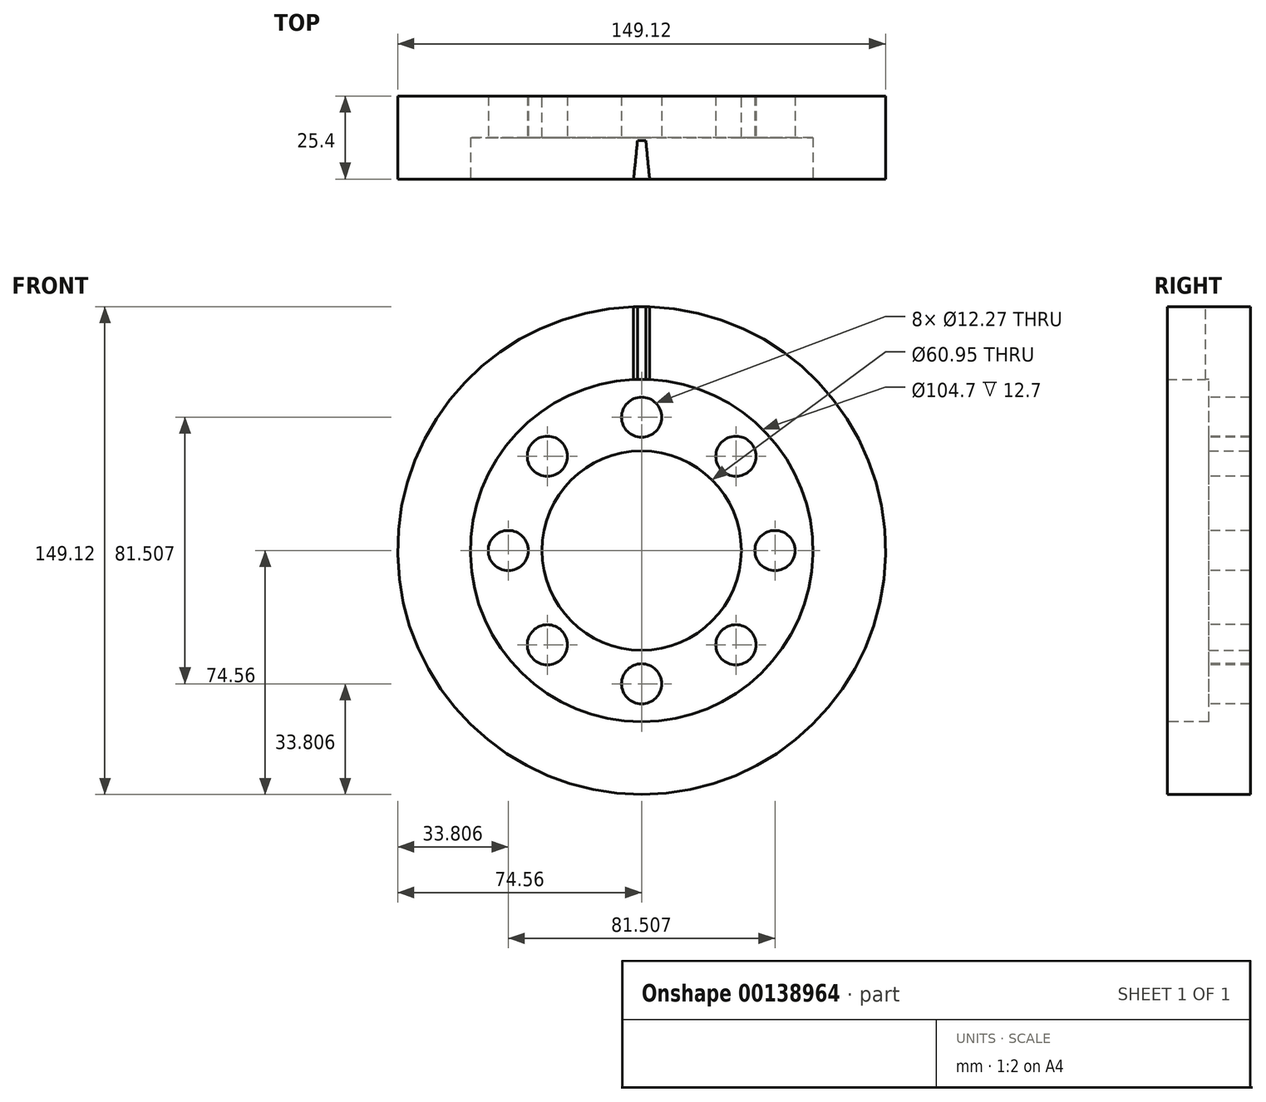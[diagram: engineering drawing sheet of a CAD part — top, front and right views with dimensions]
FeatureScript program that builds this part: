
annotation { "Feature Type Name" : "Feature", "Feature Type Description" : "" }
export const myFeature = defineFeature(function(context is Context, id is Id, definition is map)
    precondition{}
    {
        {
            var Q0;
            Q0=qCreatedBy(makeId("Front.planeOp"),FACE);
            var sketch = newSketch(context, id + "F0", { "sketchPlane" : qUnion([Q0])});
            skCircle(sketch, "E0", {"center": v(0, 0) * mm, "radius": 74.56 * mm});
            skCircle(sketch, "E1", {"center": v(0, 0) * mm, "radius": 30.48 * mm});
            skSolve(sketch);
        }
        {
            var Q0;
            Q0 = qSketchRegion(id + "F0", true);
            extrude(context, id + "F1", {"entities" : qUnion([Q0]), "depth" : 25.4 * mm});
        }
        {
            var Q0;
            Q0=makeQuery(id+"F1.opExtrude","CAP_FACE",FACE,{"disambiguationData":[OSD([sQuery(id+"F0.wireOp",EDGE,"E0"),sQuery(id+"F0.wireOp",EDGE,"E1")])],"isStart":false});
            var sketch = newSketch(context, id + "F2", { "sketchPlane" : qUnion([Q0])});
            skCircle(sketch, "E2", {"center": v(0, 0) * mm, "radius": 52.35 * mm});
            skSolve(sketch);
        }
        {
            var Q0;
            Q0 = qSketchRegion(id + "F2", true);
            extrude(context, id + "F3", {"entities" : qUnion([Q0]), "operationType" : NewBodyOperationType.REMOVE, "oppositeDirection" : true, "depth" : 12.7 * mm});
        }
        {
            var Q0;
            Q0=makeQuery(id+"F3.boolean.opBoolean","COPY",FACE,{"derivedFrom":makeQuery(id+"F3.opExtrude","CAP_FACE",FACE,{"disambiguationData":[OSD([sQuery(id+"F2.wireOp",EDGE,"E2")])],"isStart":false})});
            var sketch = newSketch(context, id + "F4", { "sketchPlane" : qUnion([Q0])});
            skCircle(sketch, "E3", {"center": v(0, 40.75) * mm, "radius": 6.13 * mm});
            skCircle(sketch, "E4.1.0", {"center": v(-28.82, 28.82) * mm, "radius": 6.13 * mm});
            skCircle(sketch, "E4.2.0", {"center": v(-40.75, 0) * mm, "radius": 6.13 * mm});
            skCircle(sketch, "E4.3.0", {"center": v(-28.82, -28.82) * mm, "radius": 6.13 * mm});
            skCircle(sketch, "E4.4.0", {"center": v(0, -40.75) * mm, "radius": 6.13 * mm});
            skCircle(sketch, "E4.5.0", {"center": v(28.82, -28.82) * mm, "radius": 6.13 * mm});
            skCircle(sketch, "E4.6.0", {"center": v(40.75, 0) * mm, "radius": 6.13 * mm});
            skCircle(sketch, "E4.7.0", {"center": v(28.82, 28.82) * mm, "radius": 6.13 * mm});
            skPoint(sketch, "E4.center", {"position": v(0, 0) * mm});
            skSolve(sketch);
        }
        {
            var Q0;
            Q0 = qSketchRegion(id + "F4", true);
            extrude(context, id + "F5", {"entities" : qUnion([Q0]), "operationType" : NewBodyOperationType.REMOVE, "oppositeDirection" : true, "depth" : 12.7 * mm});
        }
        {
            var Q0;
            Q0=qCreatedBy(makeId("Top.planeOp"),FACE);
            cPlane(context, id + "F6", {"entities" : qUnion([Q0]), "cplaneType" : CPlaneType.OFFSET, "offset" : 76.2 * mm, "width" : 152.4 * mm, "height" : 152.4 * mm});
        }
        {
            var Q0;
            Q0=qCreatedBy(id+"F6.planeOp",FACE);
            var sketch = newSketch(context, id + "F7", { "sketchPlane" : qUnion([Q0])});
            skLineSegment(sketch, "E5", {"start": v(-2.54, -26.39) * mm, "end": v(2.54, -26.39) * mm});
            skLineSegment(sketch, "E6", {"start": v(2.54, -26.39) * mm, "end": v(1.27, -13.69) * mm});
            skLineSegment(sketch, "E7", {"start": v(1.27, -13.69) * mm, "end": v(-1.27, -13.69) * mm});
            skLineSegment(sketch, "E8", {"start": v(-1.27, -13.69) * mm, "end": v(-2.54, -26.39) * mm});
            skSolve(sketch);
        }
        {
            var Q0;
            Q0 = qSketchRegion(id + "F7", true);
            extrude(context, id + "F8", {"entities" : qUnion([Q0]), "operationType" : NewBodyOperationType.REMOVE, "oppositeDirection" : true, "depth" : 25.4 * mm});
        }
        {
            var Q0;
            Q0=qCreatedBy(makeId("Top.planeOp"),FACE);
            var sketch = newSketch(context, id + "F9", { "sketchPlane" : qUnion([Q0])});
            skLineSegment(sketch, "E9", {"start": v(0, 67.37) * mm, "end": v(0, -72.36) * mm});
            skSolve(sketch);
        }
    });
